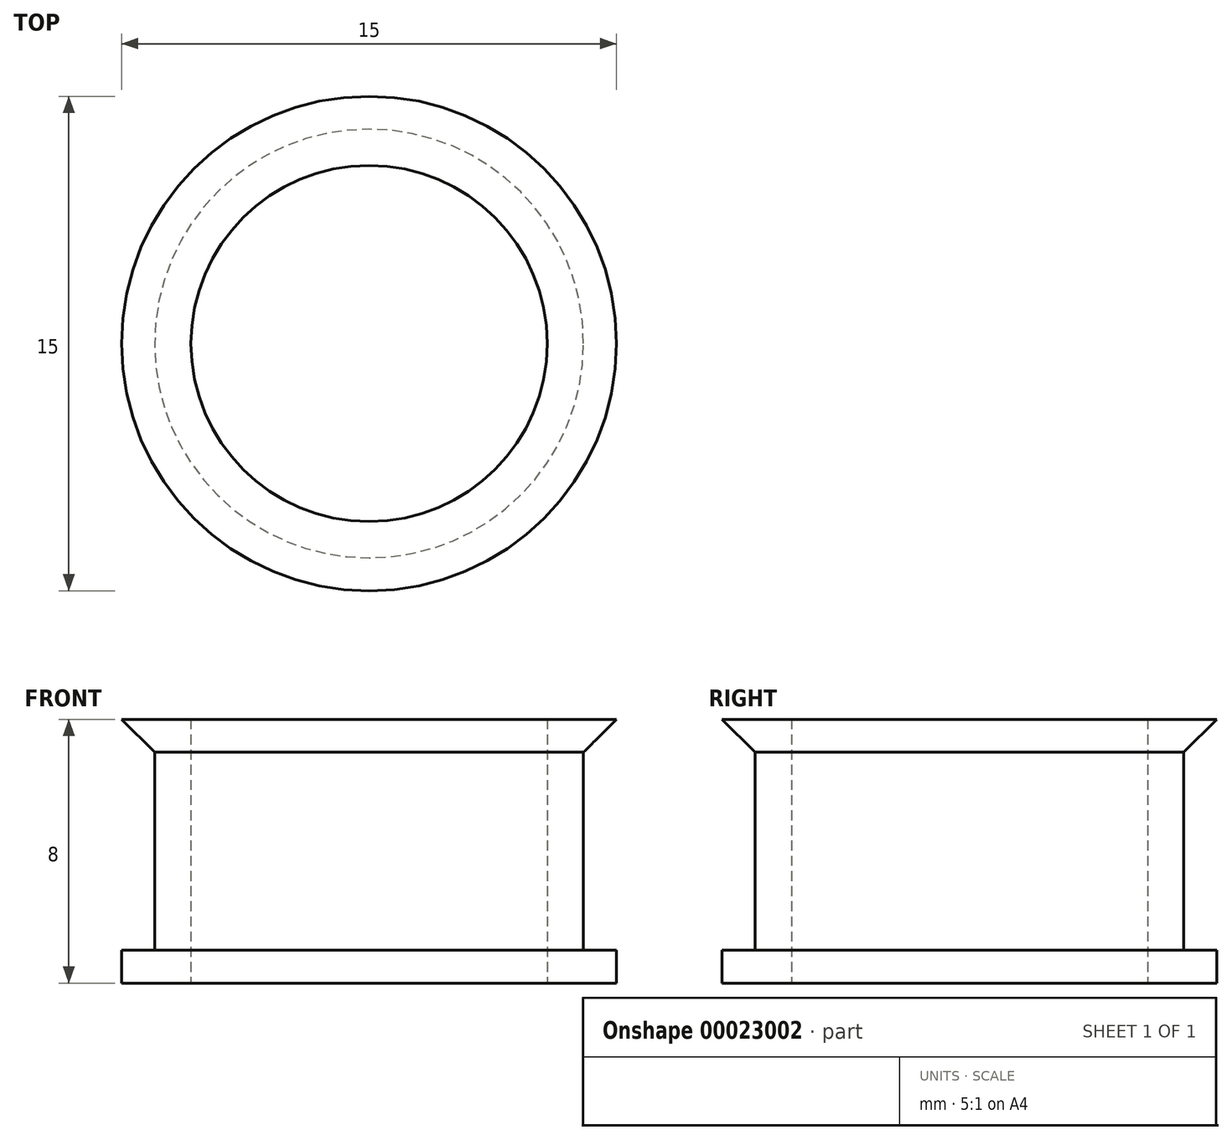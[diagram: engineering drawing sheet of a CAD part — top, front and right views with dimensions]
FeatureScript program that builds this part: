
annotation { "Feature Type Name" : "Feature", "Feature Type Description" : "" }
export const myFeature = defineFeature(function(context is Context, id is Id, definition is map)
    precondition{}
    {
        {
            var Q0;
            Q0=qCreatedBy(makeId("Top.planeOp"),FACE);
            var sketch = newSketch(context, id + "F0", { "sketchPlane" : qUnion([Q0])});
            skCircle(sketch, "E0", {"center": v(0, 0) * mm, "radius": 6.5 * mm});
            skCircle(sketch, "E1", {"center": v(0, 0) * mm, "radius": 5.4 * mm});
            skCircle(sketch, "E2", {"center": v(0, 0) * mm, "radius": 7.5 * mm});
            skSolve(sketch);
        }
        {
            var Q0;
            Q0=makeQuery(id+"F0.imprint","IMPRINT",FACE,{"disambiguationData":[TD([[makeQuery(id+"F0.imprint","IMPRINT",EDGE,{"derivedFrom":sQuery(id+"F0.wireOp",EDGE,"E0")}),1.0]])]});
            extrude(context, id + "F1", {"entities" : qUnion([Q0]), "depth" : 8 * mm});
        }
        {
            var Q0;
            Q0=makeQuery(id+"F0.imprint","IMPRINT",FACE,{"disambiguationData":[TD([[makeQuery(id+"F0.imprint","IMPRINT",EDGE,{"derivedFrom":sQuery(id+"F0.wireOp",EDGE,"E0")}),-1.0]])]});
            extrude(context, id + "F2", {"entities" : qUnion([Q0]), "operationType" : NewBodyOperationType.ADD, "depth" : 8 * mm, "hasSecondDirection" : true, "secondDirectionOppositeDirection" : false, "secondDirectionDepth" : 7 * mm});
        }
        {
            var Q0;
            Q0=makeQuery(id+"F0.imprint","IMPRINT",FACE,{"disambiguationData":[TD([[makeQuery(id+"F0.imprint","IMPRINT",EDGE,{"derivedFrom":sQuery(id+"F0.wireOp",EDGE,"E0")}),-1.0]])]});
            extrude(context, id + "F3", {"entities" : qUnion([Q0]), "operationType" : NewBodyOperationType.ADD, "depth" : 1 * mm});
        }
        {
            var Q0;
            Q0=makeQuery(id+"F2.opExtrude","CAP_EDGE",EDGE,{"disambiguationData":[OSD([sQuery(id+"F0.wireOp",EDGE,"E2")])],"isStart":true});
            chamfer(context, id + "F4", {"entities" : qUnion([Q0]), "width" : 1 * mm, "tangentPropagation" : true});
        }
    });
